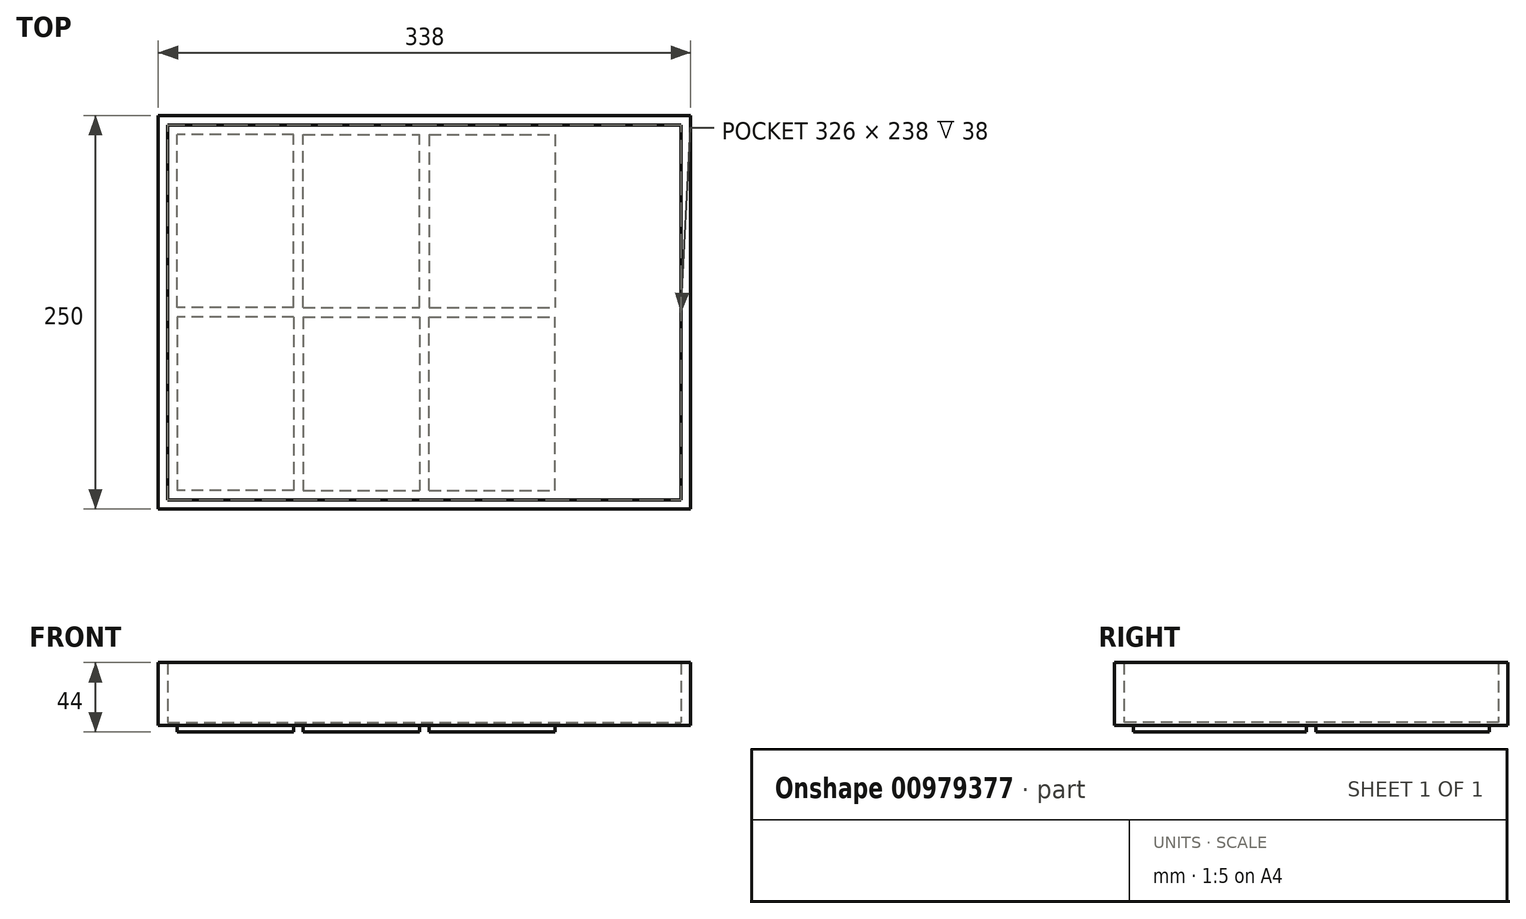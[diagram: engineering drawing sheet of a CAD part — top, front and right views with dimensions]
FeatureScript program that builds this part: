
annotation { "Feature Type Name" : "Feature", "Feature Type Description" : "" }
export const myFeature = defineFeature(function(context is Context, id is Id, definition is map)
    precondition{}
    {
        {
            var Q0;
            Q0=qCreatedBy(makeId("Top.planeOp"),FACE);
            var sketch = newSketch(context, id + "F0", { "sketchPlane" : qUnion([Q0])});
            skLineSegment(sketch, "E0.bottom", {"start": v(-3, 3) * mm, "end": v(-77, 3) * mm});
            skLineSegment(sketch, "E0.top", {"start": v(-3, 113) * mm, "end": v(-77, 113) * mm});
            skLineSegment(sketch, "E0.left", {"start": v(3, 3) * mm, "end": v(3, 113) * mm});
            skLineSegment(sketch, "E0.right", {"start": v(-77, 3) * mm, "end": v(-77, 113) * mm});
            skLineSegment(sketch, "E1.MirrorCS", {"start": v(3, 113) * mm, "end": v(77, 113) * mm});
            skLineSegment(sketch, "E2.MirrorCS", {"start": v(-3, 3) * mm, "end": v(-3, 113) * mm});
            skLineSegment(sketch, "E3.MirrorCS", {"start": v(3, 3) * mm, "end": v(77, 3) * mm});
            skLineSegment(sketch, "E4.MirrorCS", {"start": v(77, 3) * mm, "end": v(77, 113) * mm});
            skPoint(sketch, "E5.orphan", {"position": v(-3, 113) * mm});
            skLineSegment(sketch, "E6.MirrorCS", {"start": v(-3, -3) * mm, "end": v(-77, -3) * mm});
            skLineSegment(sketch, "E7.MirrorCS", {"start": v(-3, -3) * mm, "end": v(-3, -113) * mm});
            skLineSegment(sketch, "E8.MirrorCS", {"start": v(-77, -3) * mm, "end": v(-77, -113) * mm});
            skLineSegment(sketch, "E9.MirrorCS", {"start": v(3, -3) * mm, "end": v(3, -113) * mm});
            skLineSegment(sketch, "E10.MirrorCS", {"start": v(3, -3) * mm, "end": v(77, -3) * mm});
            skLineSegment(sketch, "E11.MirrorCS", {"start": v(77, -3) * mm, "end": v(77, -113) * mm});
            skLineSegment(sketch, "E12.MirrorCS", {"start": v(3, -113) * mm, "end": v(77, -113) * mm});
            skLineSegment(sketch, "E13.MirrorCS", {"start": v(-3, -113) * mm, "end": v(-77, -113) * mm});
            skLineSegment(sketch, "E14.bottom", {"start": v(83, 113) * mm, "end": v(163, 113) * mm});
            skLineSegment(sketch, "E14.top", {"start": v(83, 3) * mm, "end": v(163, 3) * mm});
            skLineSegment(sketch, "E14.left", {"start": v(83, 113) * mm, "end": v(83, 3) * mm});
            skLineSegment(sketch, "E14.right", {"start": v(163, 113) * mm, "end": v(163, 3) * mm});
            skLineSegment(sketch, "E15.MirrorCS", {"start": v(83, -3) * mm, "end": v(163, -3) * mm});
            skLineSegment(sketch, "E16.MirrorCS", {"start": v(83, -113) * mm, "end": v(83, -3) * mm});
            skLineSegment(sketch, "E17.MirrorCS", {"start": v(163, -113) * mm, "end": v(163, -3) * mm});
            skLineSegment(sketch, "E18.MirrorCS", {"start": v(83, -113) * mm, "end": v(163, -113) * mm});
            skLineSegment(sketch, "E19.bottom", {"start": v(-83, 119) * mm, "end": v(243, 119) * mm});
            skLineSegment(sketch, "E19.top", {"start": v(-83, -119) * mm, "end": v(243, -119) * mm});
            skLineSegment(sketch, "E19.left", {"start": v(-83, 119) * mm, "end": v(-83, -119) * mm});
            skLineSegment(sketch, "E19.right", {"start": v(243, 119) * mm, "end": v(243, -119) * mm});
            skLineSegment(sketch, "E20.bottom", {"start": v(-89, -125) * mm, "end": v(249, -125) * mm});
            skLineSegment(sketch, "E20.top", {"start": v(-89, 125) * mm, "end": v(249, 125) * mm});
            skLineSegment(sketch, "E20.left", {"start": v(-89, -125) * mm, "end": v(-89, 125) * mm});
            skLineSegment(sketch, "E20.right", {"start": v(249, -125) * mm, "end": v(249, 125) * mm});
            skSolve(sketch);
        }
        {
            var Q0;
            Q0=makeQuery(id+"F0.imprint","IMPRINT",FACE,{"disambiguationData":[TD([[makeQuery(id+"F0.imprint","IMPRINT",EDGE,{"derivedFrom":sQuery(id+"F0.wireOp",EDGE,"E0.bottom")}),1.0]])]});
            var Q1;
            Q1=makeQuery(id+"F0.imprint","IMPRINT",FACE,{"disambiguationData":[TD([[makeQuery(id+"F0.imprint","IMPRINT",EDGE,{"derivedFrom":sQuery(id+"F0.wireOp",EDGE,"E15.MirrorCS")}),-1.0]])]});
            var Q2;
            Q2=makeQuery(id+"F0.imprint","IMPRINT",FACE,{"disambiguationData":[TD([[makeQuery(id+"F0.imprint","IMPRINT",EDGE,{"derivedFrom":sQuery(id+"F0.wireOp",EDGE,"E14.bottom")}),-1.0]])]});
            var Q3;
            Q3=makeQuery(id+"F0.imprint","IMPRINT",FACE,{"disambiguationData":[TD([[makeQuery(id+"F0.imprint","IMPRINT",EDGE,{"derivedFrom":sQuery(id+"F0.wireOp",EDGE,"E0.left")}),-1.0]])]});
            var Q4;
            Q4=makeQuery(id+"F0.imprint","IMPRINT",FACE,{"disambiguationData":[TD([[makeQuery(id+"F0.imprint","IMPRINT",EDGE,{"derivedFrom":sQuery(id+"F0.wireOp",EDGE,"E9.MirrorCS")}),1.0]])]});
            var Q5;
            Q5=makeQuery(id+"F0.imprint","IMPRINT",FACE,{"disambiguationData":[TD([[makeQuery(id+"F0.imprint","IMPRINT",EDGE,{"derivedFrom":sQuery(id+"F0.wireOp",EDGE,"E6.MirrorCS")}),1.0]])]});
            var Q6;
            Q6=makeQuery(id+"F0.imprint","IMPRINT",FACE,{"disambiguationData":[TD([[makeQuery(id+"F0.imprint","IMPRINT",EDGE,{"derivedFrom":sQuery(id+"F0.wireOp",EDGE,"E0.bottom")}),-1.0]])]});
            extrude(context, id + "F1", {"entities" : qUnion([Q0, Q1, Q2, Q3, Q4, Q5, Q6]), "depth" : 2 * mm, "offsetDistance" : 25 * mm});
        }
        {
            var Q0;
            Q0=makeQuery(id+"F0.imprint","IMPRINT",FACE,{"disambiguationData":[TD([[makeQuery(id+"F0.imprint","IMPRINT",EDGE,{"derivedFrom":sQuery(id+"F0.wireOp",EDGE,"E15.MirrorCS")}),-1.0]])]});
            var Q1;
            Q1=makeQuery(id+"F0.imprint","IMPRINT",FACE,{"disambiguationData":[TD([[makeQuery(id+"F0.imprint","IMPRINT",EDGE,{"derivedFrom":sQuery(id+"F0.wireOp",EDGE,"E9.MirrorCS")}),1.0]])]});
            var Q2;
            Q2=makeQuery(id+"F0.imprint","IMPRINT",FACE,{"disambiguationData":[TD([[makeQuery(id+"F0.imprint","IMPRINT",EDGE,{"derivedFrom":sQuery(id+"F0.wireOp",EDGE,"E6.MirrorCS")}),1.0]])]});
            var Q3;
            Q3=makeQuery(id+"F0.imprint","IMPRINT",FACE,{"disambiguationData":[TD([[makeQuery(id+"F0.imprint","IMPRINT",EDGE,{"derivedFrom":sQuery(id+"F0.wireOp",EDGE,"E14.bottom")}),-1.0]])]});
            var Q4;
            Q4=makeQuery(id+"F0.imprint","IMPRINT",FACE,{"disambiguationData":[TD([[makeQuery(id+"F0.imprint","IMPRINT",EDGE,{"derivedFrom":sQuery(id+"F0.wireOp",EDGE,"E0.left")}),-1.0]])]});
            var Q5;
            Q5=makeQuery(id+"F0.imprint","IMPRINT",FACE,{"disambiguationData":[TD([[makeQuery(id+"F0.imprint","IMPRINT",EDGE,{"derivedFrom":sQuery(id+"F0.wireOp",EDGE,"E0.bottom")}),-1.0]])]});
            extrude(context, id + "F2", {"entities" : qUnion([Q0, Q1, Q2, Q3, Q4, Q5]), "operationType" : NewBodyOperationType.ADD, "oppositeDirection" : true, "depth" : 4 * mm, "offsetDistance" : 25 * mm});
        }
        {
            var Q0;
            Q0=makeQuery(id+"F0.imprint","IMPRINT",FACE,{"disambiguationData":[TD([[makeQuery(id+"F0.imprint","IMPRINT",EDGE,{"derivedFrom":sQuery(id+"F0.wireOp",EDGE,"E19.bottom")}),1.0]])]});
            extrude(context, id + "F3", {"entities" : qUnion([Q0]), "operationType" : NewBodyOperationType.ADD, "depth" : 40 * mm, "offsetDistance" : 25 * mm});
        }
        {
            var Q0;
            Q0=qCreatedBy(makeId("Front.planeOp"),FACE);
            cPlane(context, id + "F4", {"entities" : qUnion([Q0]), "cplaneType" : CPlaneType.OFFSET, "offset" : 125 * mm, "width" : 150 * mm, "height" : 150 * mm});
        }
    });
